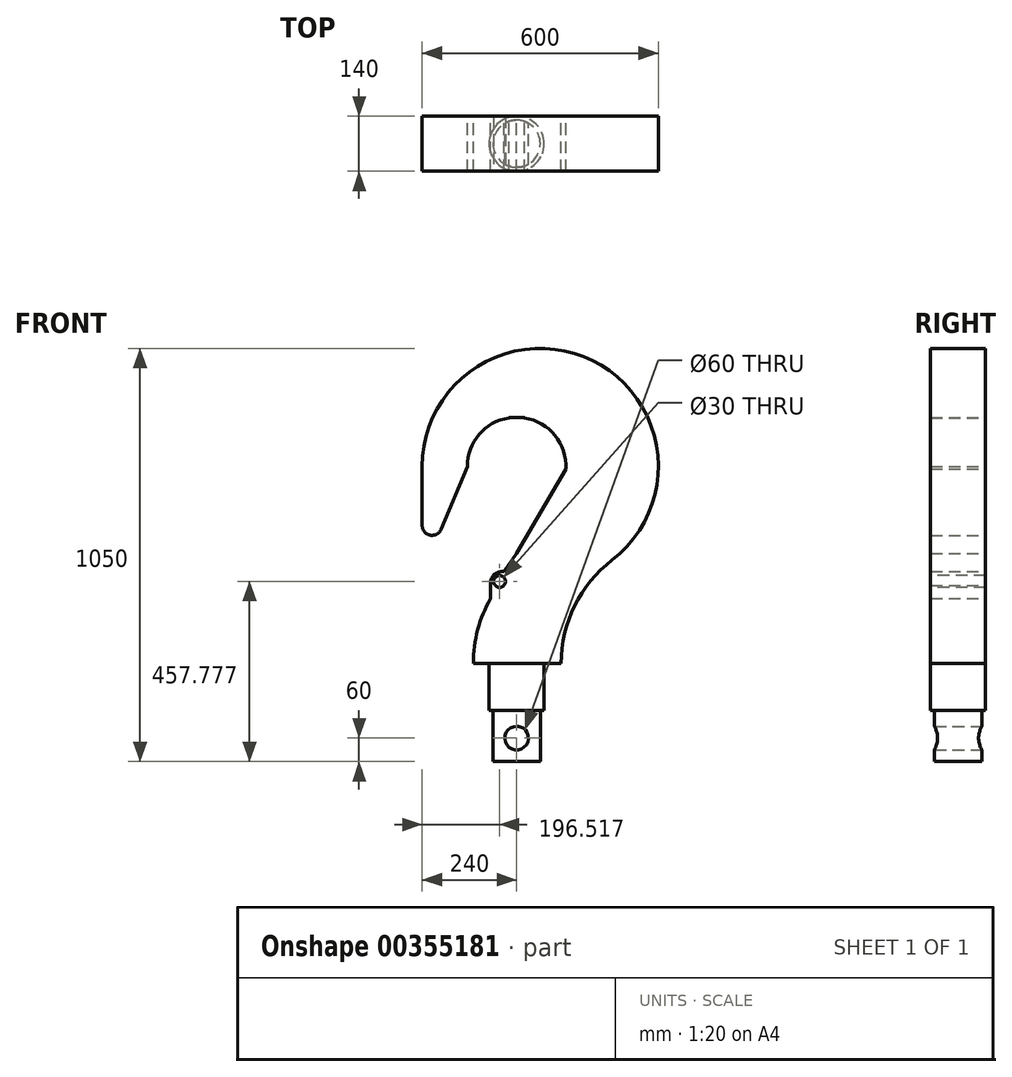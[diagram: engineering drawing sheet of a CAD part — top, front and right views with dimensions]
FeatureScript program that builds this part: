
annotation { "Feature Type Name" : "Feature", "Feature Type Description" : "" }
export const myFeature = defineFeature(function(context is Context, id is Id, definition is map)
    precondition{}
    {
        {
            var Q0;
            Q0=qCreatedBy(makeId("Front.planeOp"),FACE);
            var sketch = newSketch(context, id + "F0", { "sketchPlane" : qUnion([Q0])});
            skArc(sketch, "E0", {"start": v(242.51, 261.9) * mm, "mid": v(147.34, 146.03) * mm, "end": v(113.28, 0) * mm});
            skArc(sketch, "E1", {"start": v(-66.06, 164.53) * mm, "mid": v(-98.83, 85.15) * mm, "end": v(-110, 0) * mm});
            skLineSegment(sketch, "E2", {"start": v(0, 898.51) * mm, "end": v(0, -968.16) * mm, "construction": true});
            skArc(sketch, "E3", {"start": v(124.84, 493.61) * mm, "mid": v(97.24, 578.55) * mm, "end": v(20, 623.39) * mm});
            skArc(sketch, "E4", {"start": v(242.51, 261.9) * mm, "mid": v(192.75, 769.03) * mm, "end": v(-240, 500) * mm});
            skLineSegment(sketch, "E5", {"start": v(124.84, 493.61) * mm, "end": v(0, 278.41) * mm});
            skLineSegment(sketch, "E6", {"start": v(-607.5, 0) * mm, "end": v(1252.05, 0) * mm, "construction": true});
            skLineSegment(sketch, "E7", {"start": v(0, 500) * mm, "end": v(-349.97, 500) * mm, "construction": true});
            skLineSegment(sketch, "E8", {"start": v(-240, 500) * mm, "end": v(-125, 500) * mm});
            skArc(sketch, "E9", {"start": v(-240, 350) * mm, "mid": v(-219.93, 325.5) * mm, "end": v(-191.94, 340.33) * mm});
            skLineSegment(sketch, "E10", {"start": v(-240, 500) * mm, "end": v(-240, 350) * mm});
            skLineSegment(sketch, "E11", {"start": v(-125, 500) * mm, "end": v(-191.94, 340.33) * mm});
            skLineSegment(sketch, "E12", {"start": v(-110, 0) * mm, "end": v(113.28, 0) * mm});
            skPoint(sketch, "E13.oppositeSnap0", {"position": v(20, 623.39) * mm});
            skLineSegment(sketch, "E13.top", {"start": v(-20, 624.95) * mm, "end": v(20, 624.95) * mm});
            skLineSegment(sketch, "E13.left", {"start": v(-20, 623.39) * mm, "end": v(-20, 624.95) * mm});
            skLineSegment(sketch, "E13.right", {"start": v(20, 623.39) * mm, "end": v(20, 624.95) * mm});
            skArc(sketch, "E14.trimOffspring", {"start": v(-20, 623.39) * mm, "mid": v(-95.2, 581) * mm, "end": v(-125, 500) * mm});
            skLineSegment(sketch, "E15.trimOffspring", {"start": v(55.5, 612) * mm, "end": v(68.67, 612) * mm, "construction": true});
            skLineSegment(sketch, "E16", {"start": v(-66.06, 164.53) * mm, "end": v(-66.06, 197.07) * mm});
            skArc(sketch, "E17", {"start": v(-31.67, 232.57) * mm, "mid": v(-58.2, 223.86) * mm, "end": v(-66.06, 197.07) * mm});
            skLineSegment(sketch, "E18", {"start": v(-31.67, 232.57) * mm, "end": v(0, 278.41) * mm});
            skSolve(sketch);
        }
        {
            var Q0;
            Q0=qCreatedBy(makeId("Front.planeOp"),FACE);
            var sketch = newSketch(context, id + "F1", { "sketchPlane" : qUnion([Q0])});
            skLineSegment(sketch, "E19", {"start": v(-60, -250) * mm, "end": v(0, -250) * mm});
            skLineSegment(sketch, "E20", {"start": v(-70, 0) * mm, "end": v(0, 0) * mm});
            skLineSegment(sketch, "E21", {"start": v(0, 0) * mm, "end": v(0, -250) * mm});
            skLineSegment(sketch, "E22", {"start": v(-70, -120) * mm, "end": v(-70, 0) * mm});
            skLineSegment(sketch, "E23", {"start": v(-70, -120) * mm, "end": v(-60, -120) * mm});
            skLineSegment(sketch, "E24", {"start": v(-60, -120) * mm, "end": v(-60, -250) * mm});
            skSolve(sketch);
        }
        {
            var Q0;
            Q0=qSketchRegion(id+"F1",true);
            var Q1;
            Q1=sQuery(id+"F1.wireOp",EDGE,"E21");
            revolve(context, id + "F2", {"entities" : qUnion([Q0]), "axis" : qUnion([Q1]), "revolveType" : RevolveType.FULL});
        }
        {
            var Q0;
            Q0=makeQuery(id+"F0.imprint","IMPRINT",FACE,{"disambiguationData":[TD([[makeQuery(id+"F0.imprint","IMPRINT",EDGE,{"derivedFrom":sQuery(id+"F0.wireOp",EDGE,"E0")}),-1.0]])]});
            var Q1;
            Q1=makeQuery(id+"F0.imprint","IMPRINT",FACE,{"disambiguationData":[TD([[makeQuery(id+"F0.imprint","IMPRINT",EDGE,{"derivedFrom":sQuery(id+"F0.wireOp",EDGE,"E8")}),-1.0]])]});
            extrude(context, id + "F3", {"entities" : qUnion([Q0, Q1]), "operationType" : NewBodyOperationType.ADD, "endBound" : BoundingType.SYMMETRIC, "depth" : 140 * mm});
        }
        {
            var Q0;
            Q0=qCreatedBy(makeId("Front.planeOp"),FACE);
            var sketch = newSketch(context, id + "F4", { "sketchPlane" : qUnion([Q0])});
            skCircle(sketch, "E25", {"center": v(0, -190) * mm, "radius": 30 * mm});
            skSolve(sketch);
        }
        {
            var Q0;
            Q0 = qSketchRegion(id + "F4", true);
            extrude(context, id + "F5", {"entities" : qUnion([Q0]), "operationType" : NewBodyOperationType.REMOVE, "endBound" : BoundingType.SYMMETRIC, "depth" : 224 * mm});
        }
        {
            var Q0;
            Q0=makeQuery(id+"F3.opExtrude","CAP_FACE",FACE,{"disambiguationData":[OSD([sQuery(id+"F0.wireOp",EDGE,"E0"),sQuery(id+"F0.wireOp",EDGE,"E1"),sQuery(id+"F0.wireOp",EDGE,"E3"),sQuery(id+"F0.wireOp",EDGE,"E4"),sQuery(id+"F0.wireOp",EDGE,"E5"),sQuery(id+"F0.wireOp",EDGE,"E9"),sQuery(id+"F0.wireOp",EDGE,"E10"),sQuery(id+"F0.wireOp",EDGE,"E11"),sQuery(id+"F0.wireOp",EDGE,"E12"),sQuery(id+"F0.wireOp",EDGE,"E13.top"),sQuery(id+"F0.wireOp",EDGE,"E13.left"),sQuery(id+"F0.wireOp",EDGE,"E13.right"),sQuery(id+"F0.wireOp",EDGE,"E14.trimOffspring")])],"isStart":false});
            var sketch = newSketch(context, id + "F6", { "sketchPlane" : qUnion([Q0])});
            skCircle(sketch, "E26", {"center": v(-43.48, 207.78) * mm, "radius": 15 * mm});
            skSolve(sketch);
        }
        {
            var Q0;
            Q0 = qSketchRegion(id + "F6", true);
            var Q1;
            Q1=makeQuery(id+"F6.imprint","IMPRINT",FACE,{"disambiguationData":[TD([[makeQuery(id+"F6.imprint","IMPRINT",EDGE,{"derivedFrom":sQuery(id+"F6.wireOp",EDGE,"E26")}),1.0]])]});
            extrude(context, id + "F7", {"entities" : qUnion([Q0, Q1]), "operationType" : NewBodyOperationType.REMOVE, "endBound" : BoundingType.SYMMETRIC, "oppositeDirection" : true, "depth" : 326 * mm});
        }
    });
